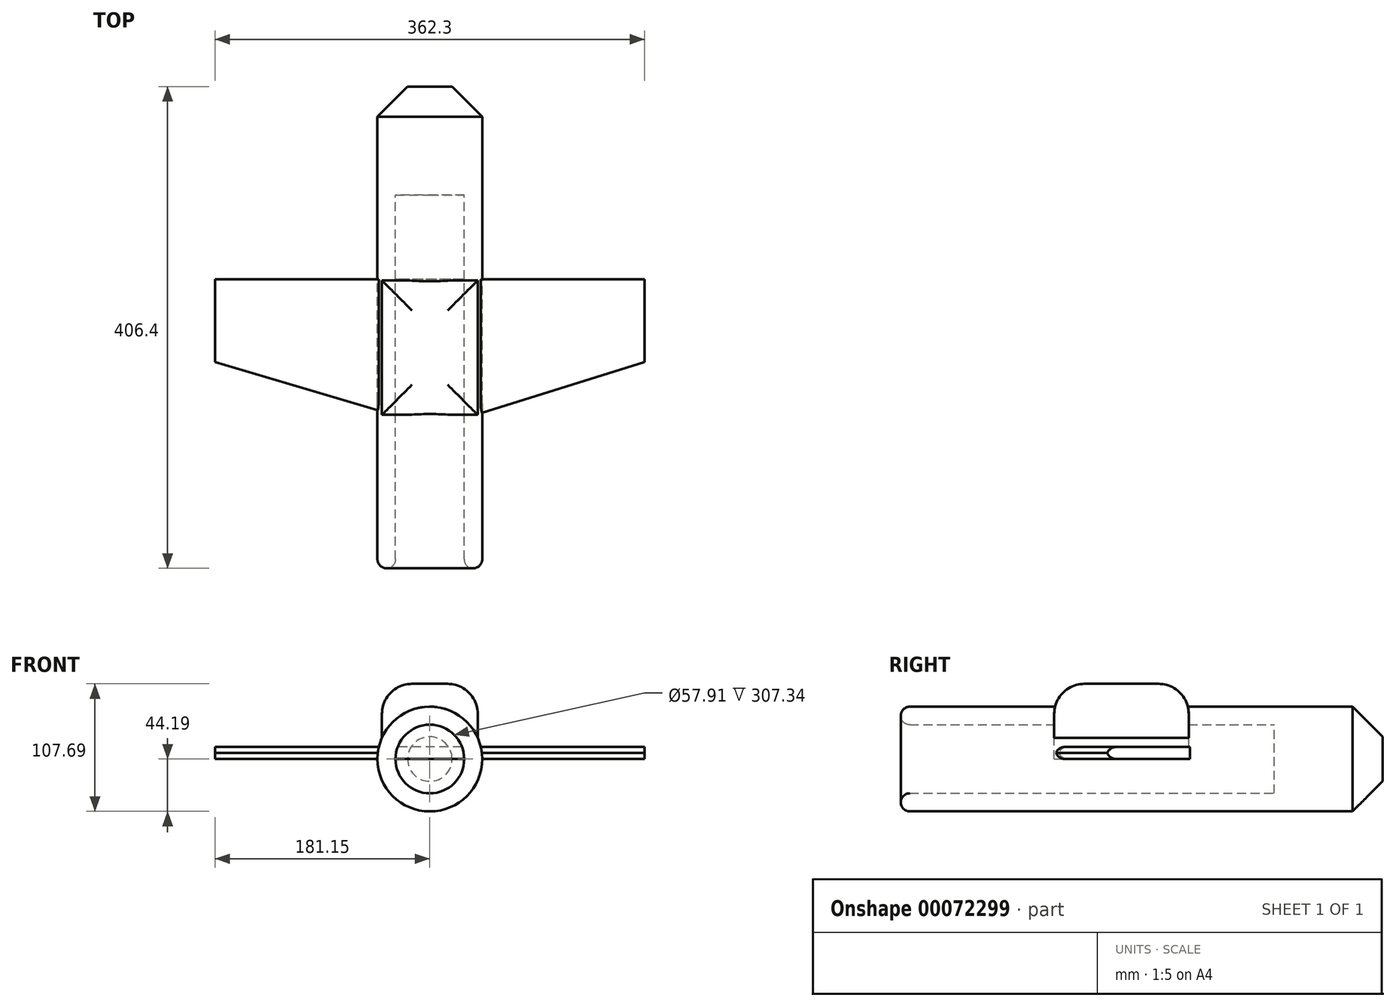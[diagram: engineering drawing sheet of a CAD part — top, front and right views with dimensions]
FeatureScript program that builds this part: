
annotation { "Feature Type Name" : "Feature", "Feature Type Description" : "" }
export const myFeature = defineFeature(function(context is Context, id is Id, definition is map)
    precondition{}
    {
        {
            var Q0;
            Q0=qCreatedBy(makeId("Front.planeOp"),FACE);
            var sketch = newSketch(context, id + "F0", { "sketchPlane" : qUnion([Q0])});
            skCircle(sketch, "E0", {"center": v(0, 0) * mm, "radius": 44.2 * mm});
            skSolve(sketch);
        }
        {
            var Q0;
            Q0=makeQuery(id+"F0.imprint","IMPRINT",FACE,{"disambiguationData":[TD([[makeQuery(id+"F0.imprint","IMPRINT",EDGE,{"derivedFrom":sQuery(id+"F0.wireOp",EDGE,"E0")}),1.0]])]});
            extrude(context, id + "F1", {"entities" : qUnion([Q0]), "depth" : 330.2 * mm});
        }
        {
            var Q0;
            Q0=makeQuery(id+"F1.opExtrude","CAP_FACE",FACE,{"disambiguationData":[OSD([sQuery(id+"F0.wireOp",EDGE,"E0")])],"isStart":false});
            shell(context, id + "F2", {"entities" : qUnion([Q0]), "thickness" : 15.24 * mm});
        }
        {
            var Q0;
            Q0=makeQuery(id+"F1.opExtrude","CAP_EDGE",EDGE,{"disambiguationData":[OSD([sQuery(id+"F0.wireOp",EDGE,"E0")])],"isStart":false});
            var Q1;
            {var subQ0=sQuery(id+"F0.wireOp",EDGE,"E0");Q1=makeQuery(id+"F2.opShell","OFFSET_EDGE",EDGE,{"disambiguationData":[OSD([subQ0]),TDD([makeQuery(id+"F1.opExtrude","CAP_EDGE",EDGE,{"disambiguationData":[OSD([subQ0])],"isStart":false})])]});}
            fillet(context, id + "F3", {"entities" : qUnion([Q0, Q1]), "radius" : 7.62 * mm, "tangentPropagation" : true, "allowEdgeOverflow" : false});
        }
        {
            var Q0;
            Q0=makeQuery(id+"F1.opExtrude","CAP_FACE",FACE,{"disambiguationData":[OSD([sQuery(id+"F0.wireOp",EDGE,"E0")])],"isStart":true});
            extrude(context, id + "F4", {"entities" : qUnion([Q0]), "operationType" : NewBodyOperationType.ADD, "depth" : 76.2 * mm});
        }
        {
            var Q0;
            Q0=makeQuery(id+"F4.opExtrude","CAP_FACE",FACE,{"disambiguationData":[OSD([sQuery(id+"F0.wireOp",EDGE,"E0")])],"isStart":false});
            chamfer(context, id + "F5", {"entities" : qUnion([Q0]), "width" : 25.4 * mm, "tangentPropagation" : true});
        }
        {
            var Q0;
            Q0=qCreatedBy(makeId("Top.planeOp"),FACE);
            var sketch = newSketch(context, id + "F6", { "sketchPlane" : qUnion([Q0])});
            skLineSegment(sketch, "E1.rect.bottom", {"start": v(40.43, -200.76) * mm, "end": v(-40.43, -200.76) * mm});
            skLineSegment(sketch, "E1.rect.top", {"start": v(40.43, -87.28) * mm, "end": v(-40.43, -87.28) * mm});
            skLineSegment(sketch, "E1.rect.left", {"start": v(40.43, -200.76) * mm, "end": v(40.43, -87.28) * mm});
            skLineSegment(sketch, "E1.rect.right", {"start": v(-40.43, -200.76) * mm, "end": v(-40.43, -87.28) * mm});
            skPoint(sketch, "E1.rect.middle", {"position": v(0, -144.02) * mm});
            skSolve(sketch);
        }
        {
            var Q0;
            Q0 = qSketchRegion(id + "F6", true);
            extrude(context, id + "F7", {"entities" : qUnion([Q0]), "operationType" : NewBodyOperationType.ADD, "depth" : 63.5 * mm});
        }
        {
            var Q0;
            Q0=makeQuery(id+"F7.opExtrude","CAP_EDGE",EDGE,{"disambiguationData":[OSD([sQuery(id+"F6.wireOp",EDGE,"E1.rect.left")])],"isStart":false});
            var Q1;
            Q1=makeQuery(id+"F7.opExtrude","CAP_EDGE",EDGE,{"disambiguationData":[OSD([sQuery(id+"F6.wireOp",EDGE,"E1.rect.top")])],"isStart":false});
            var Q2;
            Q2=makeQuery(id+"F7.opExtrude","CAP_EDGE",EDGE,{"disambiguationData":[OSD([sQuery(id+"F6.wireOp",EDGE,"E1.rect.bottom")])],"isStart":false});
            var Q3;
            Q3=makeQuery(id+"F7.opExtrude","CAP_EDGE",EDGE,{"disambiguationData":[OSD([sQuery(id+"F6.wireOp",EDGE,"E1.rect.right")])],"isStart":false});
            fillet(context, id + "F8", {"entities" : qUnion([Q0, Q1, Q2, Q3]), "radius" : 25.4 * mm, "tangentPropagation" : true, "allowEdgeOverflow" : false});
        }
        {
            var Q0;
            Q0=qCreatedBy(makeId("Top.planeOp"),FACE);
            var sketch = newSketch(context, id + "F9", { "sketchPlane" : qUnion([Q0])});
            skLineSegment(sketch, "E2.rect.bottom", {"start": v(181.15, -86.34) * mm, "end": v(-181.15, -86.34) * mm});
            skLineSegment(sketch, "E2.rect.top", {"start": v(181.15, -156.48) * mm, "end": v(-181.15, -156.48) * mm});
            skLineSegment(sketch, "E2.rect.left", {"start": v(181.15, -86.34) * mm, "end": v(181.15, -156.48) * mm});
            skLineSegment(sketch, "E2.rect.right", {"start": v(-181.15, -86.34) * mm, "end": v(-181.15, -156.48) * mm});
            skPoint(sketch, "E2.rect.middle", {"position": v(0, -121.4) * mm});
            skLineSegment(sketch, "E3", {"start": v(-40.54, -198.23) * mm, "end": v(-181.15, -156.48) * mm});
            skLineSegment(sketch, "E4", {"start": v(40.45, -200.73) * mm, "end": v(181.15, -156.48) * mm});
            skLineSegment(sketch, "E5", {"start": v(-40.54, -156.48) * mm, "end": v(-40.54, -198.23) * mm});
            skLineSegment(sketch, "E6", {"start": v(40.45, -200.73) * mm, "end": v(40.45, -156.48) * mm});
            skSolve(sketch);
        }
        {
            var Q0;
            Q0 = qSketchRegion(id + "F9", true);
            extrude(context, id + "F10", {"entities" : qUnion([Q0]), "operationType" : NewBodyOperationType.ADD, "depth" : 10.16 * mm});
        }
        {
            var Q0;
            Q0=makeQuery(id+"F10.opExtrude","CAP_EDGE",EDGE,{"disambiguationData":[OSD([sQuery(id+"F9.wireOp",EDGE,"E4")])],"isStart":true});
            var Q1;
            Q1=makeQuery(id+"F10.opExtrude","CAP_EDGE",EDGE,{"disambiguationData":[OSD([sQuery(id+"F9.wireOp",EDGE,"E4")])],"isStart":false});
            var Q2;
            Q2=makeQuery(id+"F10.opExtrude","CAP_EDGE",EDGE,{"disambiguationData":[OSD([sQuery(id+"F9.wireOp",EDGE,"E3")])],"isStart":false});
            var Q3;
            Q3=makeQuery(id+"F10.opExtrude","CAP_EDGE",EDGE,{"disambiguationData":[OSD([sQuery(id+"F9.wireOp",EDGE,"E3")])],"isStart":true});
            fillet(context, id + "F11", {"entities" : qUnion([Q0, Q1, Q2, Q3]), "radius" : 7.62 * mm, "tangentPropagation" : true, "allowEdgeOverflow" : false});
        }
    });
